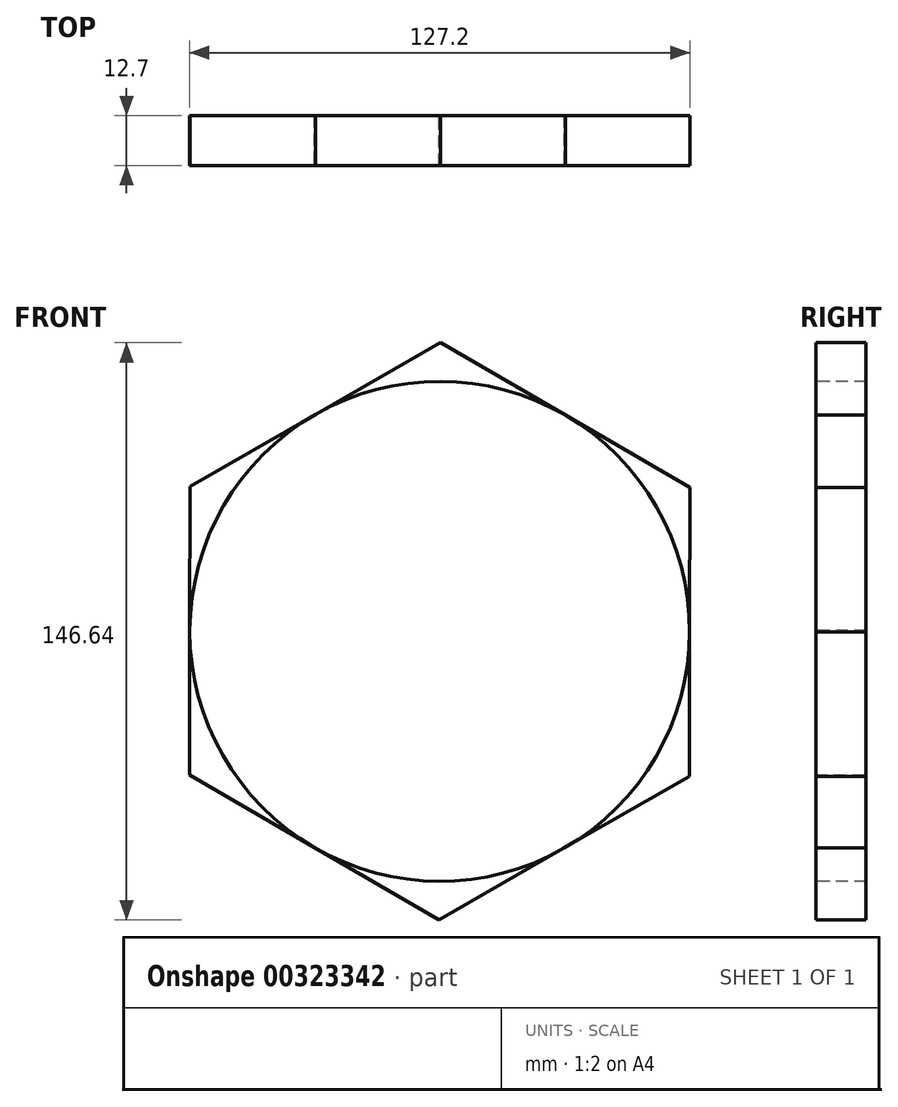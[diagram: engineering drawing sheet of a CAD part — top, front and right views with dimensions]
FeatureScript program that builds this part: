
annotation { "Feature Type Name" : "Feature", "Feature Type Description" : "" }
export const myFeature = defineFeature(function(context is Context, id is Id, definition is map)
    precondition{}
    {
        {
            var Q0;
            Q0=qCreatedBy(makeId("Front.planeOp"),FACE);
            var sketch = newSketch(context, id + "F0", { "sketchPlane" : qUnion([Q0])});
            skCircle(sketch, "E0", {"center": v(0, 0) * mm, "radius": 63.5 * mm});
            skCircle(sketch, "E1.cCircle", {"center": v(0, 0) * mm, "radius": 63.5 * mm, "construction": true});
            skLineSegment(sketch, "E1.0", {"start": v(-63.4, 36.84) * mm, "end": v(0.2, 73.32) * mm});
            skLineSegment(sketch, "E1.1", {"start": v(0.2, 73.32) * mm, "end": v(63.6, 36.49) * mm});
            skLineSegment(sketch, "E1.2", {"start": v(63.6, 36.49) * mm, "end": v(63.4, -36.84) * mm});
            skLineSegment(sketch, "E1.3", {"start": v(63.4, -36.84) * mm, "end": v(-0.2, -73.32) * mm});
            skLineSegment(sketch, "E1.4", {"start": v(-0.2, -73.32) * mm, "end": v(-63.6, -36.49) * mm});
            skLineSegment(sketch, "E1.5", {"start": v(-63.6, -36.49) * mm, "end": v(-63.4, 36.84) * mm});
            skPoint(sketch, "E1.0.midPoint", {"position": v(-31.6, 55.08) * mm});
            skSolve(sketch);
        }
        {
            var Q0;
            Q0 = qSketchRegion(id + "F0", true);
            extrude(context, id + "F1", {"entities" : qUnion([Q0]), "depth" : 12.7 * mm});
        }
        {
            var Q0;
            Q0=makeQuery(id+"F1.opExtrude","CAP_FACE",FACE,{"disambiguationData":[OSD([sQuery(id+"F0.wireOp",EDGE,"E1.0"),sQuery(id+"F0.wireOp",EDGE,"E1.1"),sQuery(id+"F0.wireOp",EDGE,"E1.2"),sQuery(id+"F0.wireOp",EDGE,"E1.3"),sQuery(id+"F0.wireOp",EDGE,"E1.4"),sQuery(id+"F0.wireOp",EDGE,"E1.5")])],"isStart":false});
            var sketch = newSketch(context, id + "F2", { "sketchPlane" : qUnion([Q0])});
            skCircle(sketch, "E2", {"center": v(0, 0) * mm, "radius": 63.5 * mm});
            skSolve(sketch);
        }
        {
            var Q0;
            {var subQ0=sQuery(id+"F2.wireOp",EDGE,"E2");var subQ4=makeQuery(id+"F2.imprint","INTERSECT",VERTEX,{"derivedFrom":[makeQuery(id+"F1.opExtrude","CAP_EDGE",EDGE,{"disambiguationData":[OSD([sQuery(id+"F0.wireOp",EDGE,"E1.0")])],"isStart":false}),subQ0]});Q0=makeQuery(id+"F2.imprint","IMPRINT",FACE,{"disambiguationData":[TD([[makeQuery(id+"F2.imprint","IMPRINT",EDGE,{"disambiguationData":[TD([[subQ4,1.0]])],"derivedFrom":subQ0}),1.0]])]});}
            extrude(context, id + "F3", {"entities" : qUnion([Q0]), "operationType" : NewBodyOperationType.REMOVE, "endBound" : BoundingType.THROUGH_ALL, "oppositeDirection" : true, "depth" : 25.4 * mm});
        }
    });
